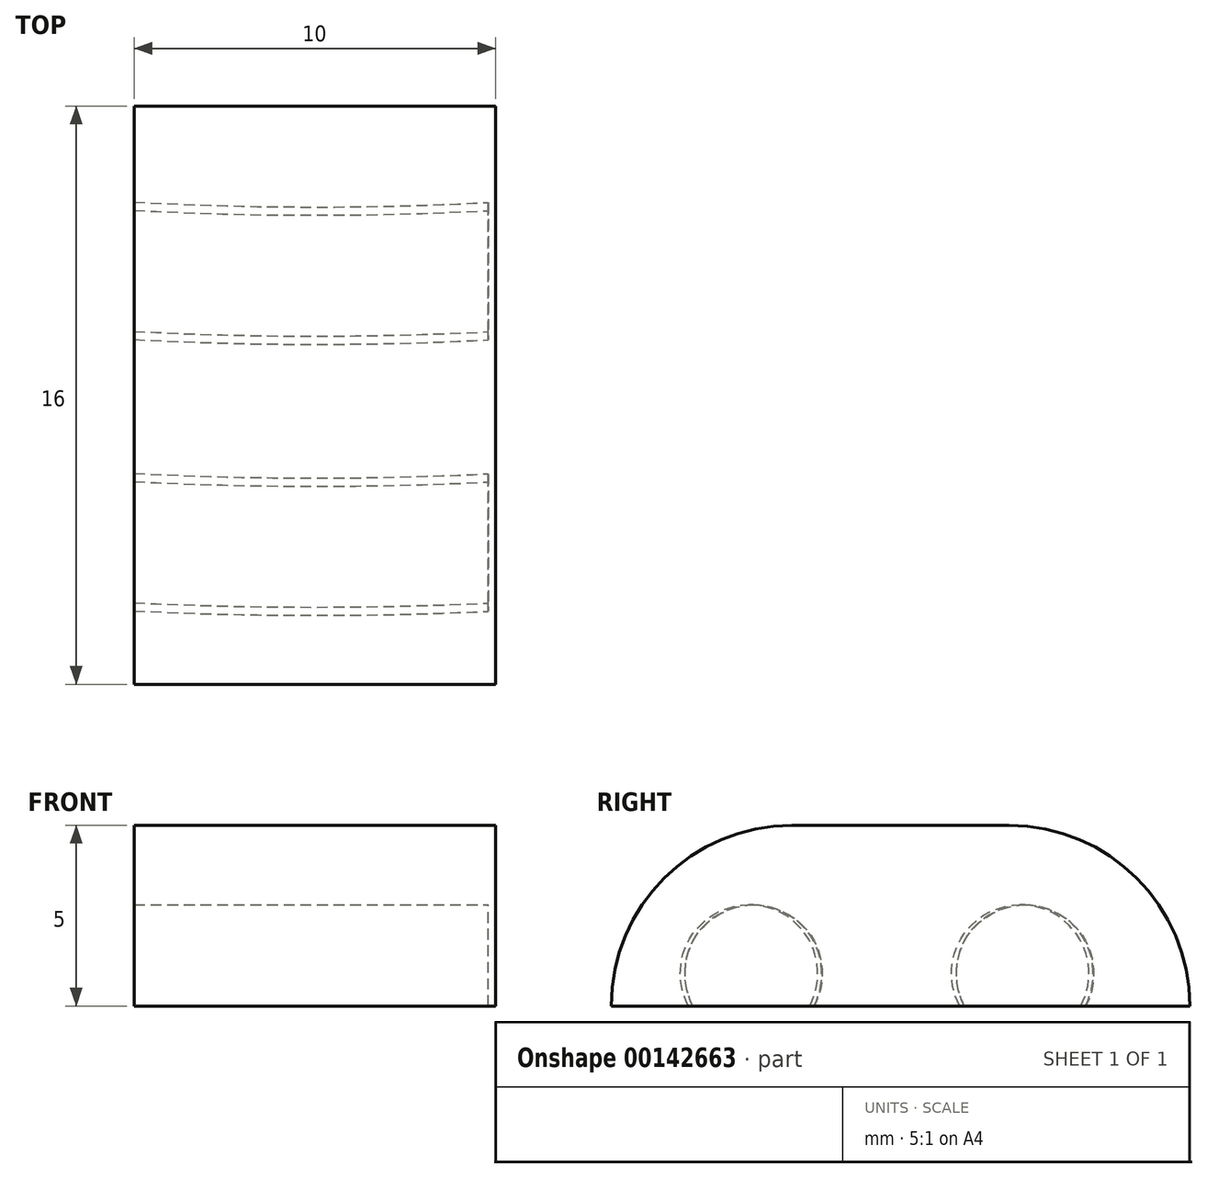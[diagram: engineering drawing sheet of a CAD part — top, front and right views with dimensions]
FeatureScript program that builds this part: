
annotation { "Feature Type Name" : "Feature", "Feature Type Description" : "" }
export const myFeature = defineFeature(function(context is Context, id is Id, definition is map)
    precondition{}
    {
        {
            var Q0;
            Q0=qCreatedBy(makeId("Front.planeOp"),FACE);
            var sketch = newSketch(context, id + "F0", { "sketchPlane" : qUnion([Q0])});
            skCircle(sketch, "E0", {"center": v(-92.5, 0) * mm, "radius": 1.9 * mm});
            skSolve(sketch);
        }
        {
            var Q0;
            Q0=qCreatedBy(makeId("Top.planeOp"),FACE);
            var sketch = newSketch(context, id + "F1", { "sketchPlane" : qUnion([Q0])});
            skPoint(sketch, "E1.0", {"position": v(-92.5, 0) * mm});
            skCircle(sketch, "E2", {"center": v(0, 0) * mm, "radius": 92.5 * mm});
            skSolve(sketch);
        }
        {
            var Q0;
            Q0=qCreatedBy(makeId("Front.planeOp"),FACE);
            var sketch = newSketch(context, id + "F2", { "sketchPlane" : qUnion([Q0])});
            skCircle(sketch, "E3", {"center": v(-100, 0) * mm, "radius": 1.9 * mm});
            skSolve(sketch);
        }
        {
            var Q0;
            Q0=qCreatedBy(makeId("Top.planeOp"),FACE);
            var sketch = newSketch(context, id + "F3", { "sketchPlane" : qUnion([Q0])});
            skPoint(sketch, "E4.0", {"position": v(-100, 0) * mm});
            skCircle(sketch, "E5", {"center": v(0, 0) * mm, "radius": 100 * mm, "construction": true});
            skSolve(sketch);
        }
        {
            var Q0;
            Q0=qCreatedBy(makeId("Top.planeOp"),FACE);
            cPlane(context, id + "F4", {"entities" : qUnion([Q0]), "cplaneType" : CPlaneType.OFFSET, "offset" : ((3.4 / 2) + 2.4) * mm, "width" : 150 * mm, "height" : 150 * mm});
        }
        {
            var Q0;
            Q0=qCreatedBy(id+"F4.planeOp",FACE);
            var sketch = newSketch(context, id + "F5", { "sketchPlane" : qUnion([Q0])});
            skLineSegment(sketch, "E6.bottom", {"start": v(5, -103.81) * mm, "end": v(-5, -103.81) * mm});
            skLineSegment(sketch, "E6.top", {"start": v(5, -87.81) * mm, "end": v(-5, -87.81) * mm});
            skLineSegment(sketch, "E6.left", {"start": v(5, -103.81) * mm, "end": v(5, -87.81) * mm});
            skLineSegment(sketch, "E6.right", {"start": v(-5, -103.81) * mm, "end": v(-5, -87.81) * mm});
            skPoint(sketch, "E6.middle", {"position": v(0, -95.81) * mm});
            skSolve(sketch);
        }
        {
            var Q0;
            Q0=qSketchRegion(id+"F5",true);
            extrude(context, id + "F6", {"entities" : qUnion([Q0]), "oppositeDirection" : true, "depth" : ((3.4 + 2.4) - .8) * mm});
        }
        {
            var Q0;
            Q0=qSketchRegion(id+"F0",true);
            var Q1;
            Q1=sQuery(id+"F1.wireOp",EDGE,"E2");
            revolve(context, id + "F7", {"operationType" : NewBodyOperationType.REMOVE, "entities" : qUnion([Q0]), "axis" : qUnion([Q1]), "revolveType" : RevolveType.FULL});
        }
        {
            var Q0;
            Q0=qSketchRegion(id+"F2",true);
            var Q1;
            Q1=sQuery(id+"F3.wireOp",EDGE,"E5");
            revolve(context, id + "F8", {"operationType" : NewBodyOperationType.REMOVE, "entities" : qUnion([Q0]), "axis" : qUnion([Q1]), "revolveType" : RevolveType.FULL});
        }
        {
            var Q0;
            Q0=makeQuery(id+"F6.opExtrude","CAP_EDGE",EDGE,{"disambiguationData":[OSD([sQuery(id+"F5.wireOp",EDGE,"E6.bottom")])],"isStart":true});
            var Q1;
            Q1=makeQuery(id+"F6.opExtrude","CAP_EDGE",EDGE,{"disambiguationData":[OSD([sQuery(id+"F5.wireOp",EDGE,"E6.top")])],"isStart":true});
            fillet(context, id + "F9", {"entities" : qUnion([Q0, Q1]), "radius" : 5 * mm, "tangentPropagation" : true, "allowEdgeOverflow" : false});
        }
        {
            var Q0;
            Q0=makeQuery(id+"F6.opExtrude","SWEPT_FACE",FACE,{"disambiguationData":[OSD([sQuery(id+"F5.wireOp",EDGE,"E6.left")])]});
            var sketch = newSketch(context, id + "F10", { "sketchPlane" : qUnion([Q0])});
            skArc(sketch, "E7.0", {"start": v(-98.81, 4.1) * mm, "mid": v(-102.35, 2.64) * mm, "end": v(-103.81, -0.9) * mm});
            skLineSegment(sketch, "E8.0", {"start": v(-98.81, 4.1) * mm, "end": v(-92.81, 4.1) * mm});
            skArc(sketch, "E9.0", {"start": v(-87.81, -0.9) * mm, "mid": v(-89.28, 2.64) * mm, "end": v(-92.81, 4.1) * mm});
            skLineSegment(sketch, "E10", {"start": v(-103.81, -0.9) * mm, "end": v(-87.81, -0.9) * mm});
            skSolve(sketch);
        }
        {
            var Q0;
            Q0=qSketchRegion(id+"F10",true);
            extrude(context, id + "F11", {"entities" : qUnion([Q0]), "operationType" : NewBodyOperationType.ADD, "oppositeDirection" : true, "depth" : 0.2 * mm});
        }
    });
